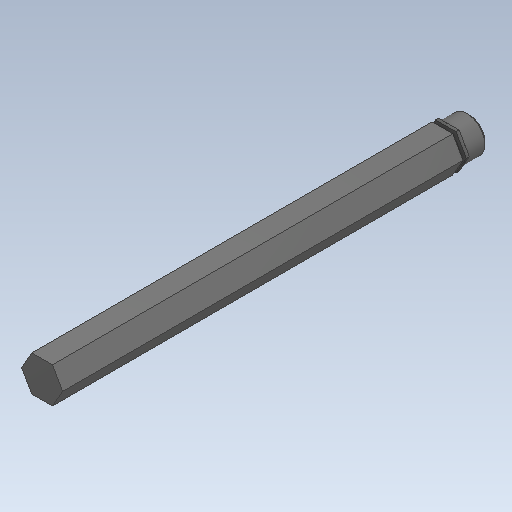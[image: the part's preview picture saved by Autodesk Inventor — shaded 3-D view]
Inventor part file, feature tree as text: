
AUTODESK INVENTOR PART (.ipt)
format: ipt  version: 2020 (Build 240168000, 168)  size: 99,328 bytes
history: native  units: in
note: dims shown in document units (in); Inventor stores cm internally (conversion verified against a paired STEP export)
features: chamfer x1
ambient origin geometry x8: Origin, YZ Plane, XZ Plane, XY Plane, X Axis, Y Axis, Z Axis, Center Point
bodies: Solid1 (feature_tree)
feature tree (1):
  chamfer  "Chamfer1"  [1 undecoded]
note: 1 required parameter value undecoded (feature->parameter linkage not recoverable at this tier; creation-order binding heuristic only, values carry confidence <= 0.55)
